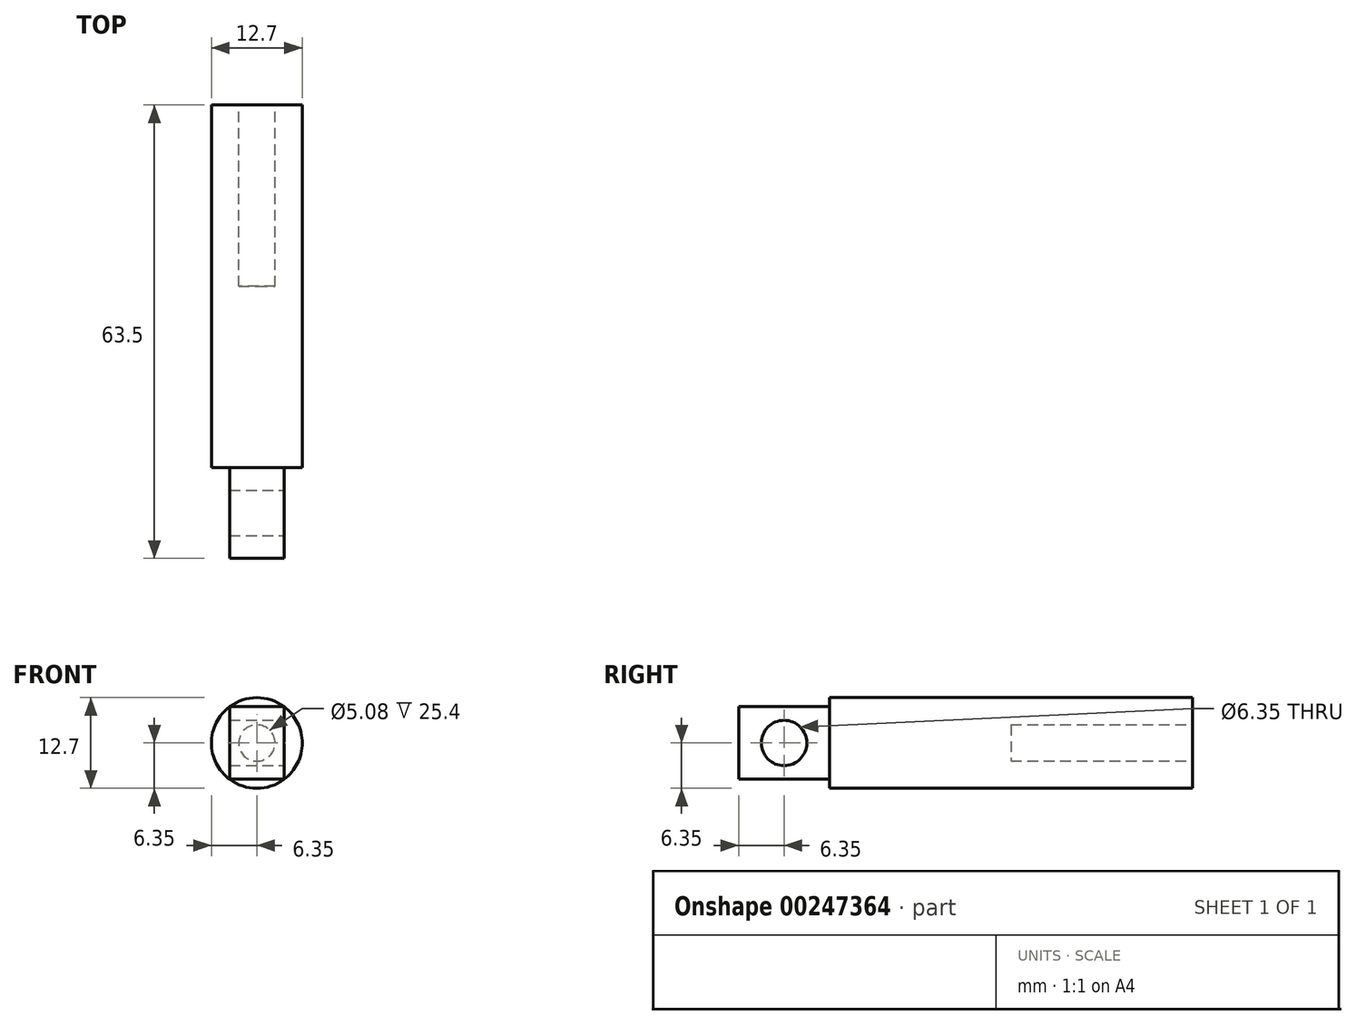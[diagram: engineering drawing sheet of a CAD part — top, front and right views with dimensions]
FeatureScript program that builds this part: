
annotation { "Feature Type Name" : "Feature", "Feature Type Description" : "" }
export const myFeature = defineFeature(function(context is Context, id is Id, definition is map)
    precondition{}
    {
        {
            var Q0;
            Q0=qCreatedBy(makeId("Front.planeOp"),FACE);
            var sketch = newSketch(context, id + "F0", { "sketchPlane" : qUnion([Q0])});
            skCircle(sketch, "E0", {"center": v(0, 0) * mm, "radius": 6.35 * mm});
            skSolve(sketch);
        }
        {
            var Q0;
            Q0 = qSketchRegion(id + "F0", true);
            extrude(context, id + "F1", {"entities" : qUnion([Q0]), "depth" : 63.5 * mm});
        }
        {
            var Q0;
            Q0=makeQuery(id+"F1.opExtrude","CAP_FACE",FACE,{"disambiguationData":[OSD([sQuery(id+"F0.wireOp",EDGE,"E0")])],"isStart":false});
            var sketch = newSketch(context, id + "F2", { "sketchPlane" : qUnion([Q0])});
            skCircle(sketch, "E1", {"center": v(0, 0) * mm, "radius": 6.35 * mm});
            skLineSegment(sketch, "E2", {"start": v(0, 0) * mm, "end": v(0, 5.08) * mm});
            skLineSegment(sketch, "E3", {"start": v(0, 5.08) * mm, "end": v(3.81, 5.08) * mm});
            skLineSegment(sketch, "E4", {"start": v(3.81, 5.08) * mm, "end": v(3.81, -5.08) * mm});
            skLineSegment(sketch, "E5", {"start": v(3.81, -5.08) * mm, "end": v(-3.81, -5.08) * mm});
            skLineSegment(sketch, "E6", {"start": v(-3.81, -5.08) * mm, "end": v(-3.81, 5.08) * mm});
            skLineSegment(sketch, "E7", {"start": v(-3.81, 5.08) * mm, "end": v(0, 5.08) * mm});
            skSolve(sketch);
        }
        {
            var Q0;
            {var subQ0=sQuery(id+"F2.wireOp",EDGE,"E3");Q0=makeQuery(id+"F2.imprint","IMPRINT",FACE,{"disambiguationData":[TD([[makeQuery(id+"F2.imprint","IMPRINT",EDGE,{"derivedFrom":subQ0}),1.0]])]});}
            var Q1;
            {var subQ0=sQuery(id+"F2.wireOp",EDGE,"E5");Q1=makeQuery(id+"F2.imprint","IMPRINT",FACE,{"disambiguationData":[TD([[makeQuery(id+"F2.imprint","IMPRINT",EDGE,{"derivedFrom":subQ0}),1.0]])]});}
            var Q2;
            {var subQ0=sQuery(id+"F2.wireOp",EDGE,"E4");Q2=makeQuery(id+"F2.imprint","IMPRINT",FACE,{"disambiguationData":[TD([[makeQuery(id+"F2.imprint","IMPRINT",EDGE,{"derivedFrom":subQ0}),1.0]])]});}
            var Q3;
            {var subQ0=sQuery(id+"F2.wireOp",EDGE,"E6");Q3=makeQuery(id+"F2.imprint","IMPRINT",FACE,{"disambiguationData":[TD([[makeQuery(id+"F2.imprint","IMPRINT",EDGE,{"derivedFrom":subQ0}),1.0]])]});}
            extrude(context, id + "F3", {"entities" : qUnion([Q0, Q1, Q2, Q3]), "operationType" : NewBodyOperationType.REMOVE, "oppositeDirection" : true, "depth" : 12.7 * mm});
        }
        {
            var Q0;
            Q0=makeQuery(id+"F3.boolean.opBoolean","COPY",FACE,{"derivedFrom":makeQuery(id+"F3.opExtrude","SWEPT_FACE",FACE,{"disambiguationData":[OSD([sQuery(id+"F2.wireOp",EDGE,"E4")])]})});
            var sketch = newSketch(context, id + "F4", { "sketchPlane" : qUnion([Q0])});
            skCircle(sketch, "E8", {"center": v(-57.15, 0) * mm, "radius": 3.18 * mm});
            skSolve(sketch);
        }
        {
            var Q0;
            Q0 = qSketchRegion(id + "F4", true);
            extrude(context, id + "F5", {"entities" : qUnion([Q0]), "operationType" : NewBodyOperationType.REMOVE, "oppositeDirection" : true, "depth" : 25.4 * mm});
        }
        {
            var Q0;
            Q0=makeQuery(id+"F1.opExtrude","CAP_FACE",FACE,{"disambiguationData":[OSD([sQuery(id+"F0.wireOp",EDGE,"E0")])],"isStart":true});
            var sketch = newSketch(context, id + "F6", { "sketchPlane" : qUnion([Q0])});
            skCircle(sketch, "E9", {"center": v(0, 0) * mm, "radius": 2.54 * mm});
            skSolve(sketch);
        }
        {
            var Q0;
            Q0 = qSketchRegion(id + "F6", true);
            extrude(context, id + "F7", {"entities" : qUnion([Q0]), "operationType" : NewBodyOperationType.REMOVE, "oppositeDirection" : true, "depth" : 25.4 * mm});
        }
    });
